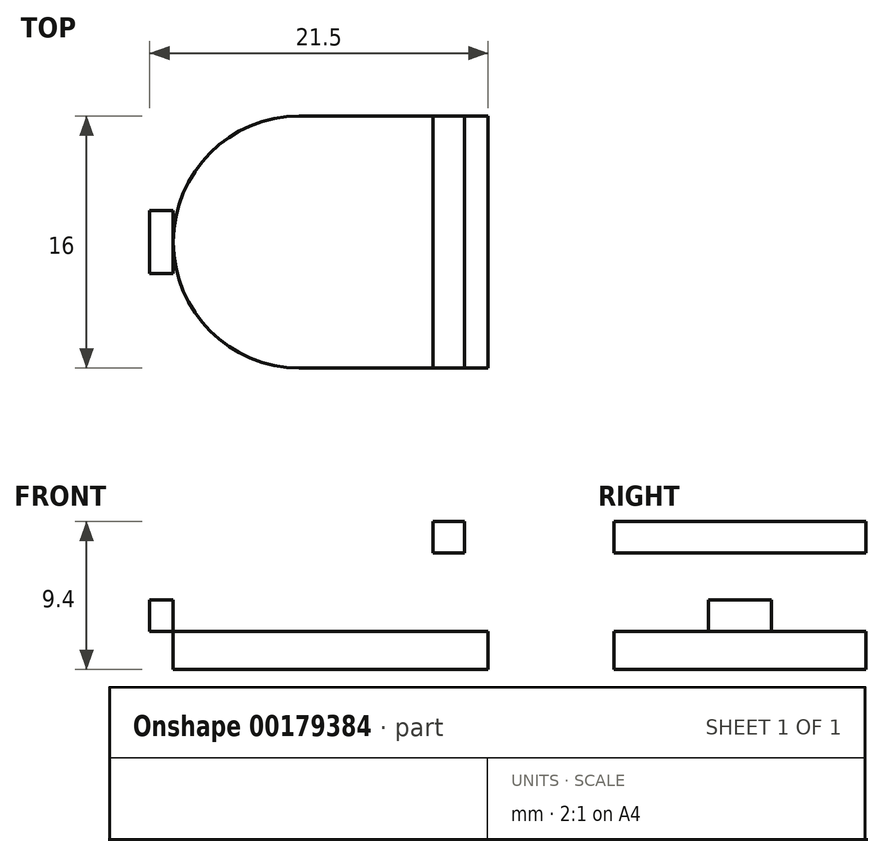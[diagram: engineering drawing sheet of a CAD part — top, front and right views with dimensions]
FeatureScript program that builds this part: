
annotation { "Feature Type Name" : "Feature", "Feature Type Description" : "" }
export const myFeature = defineFeature(function(context is Context, id is Id, definition is map)
    precondition{}
    {
        {
            var Q0;
            Q0=qCreatedBy(makeId("Front.planeOp"),FACE);
            var sketch = newSketch(context, id + "F0", { "sketchPlane" : qUnion([Q0])});
            skLineSegment(sketch, "E0.bottom", {"start": v(6, -1.2) * mm, "end": v(-6, -1.2) * mm});
            skLineSegment(sketch, "E0.top", {"start": v(6, 1.2) * mm, "end": v(-6, 1.2) * mm});
            skLineSegment(sketch, "E0.left", {"start": v(6, -1.2) * mm, "end": v(6, 1.2) * mm});
            skLineSegment(sketch, "E0.right", {"start": v(-6, -1.2) * mm, "end": v(-6, 1.2) * mm});
            skPoint(sketch, "E0.middle", {"position": v(0, 0) * mm});
            skLineSegment(sketch, "E1.bottom", {"start": v(6, 1.2) * mm, "end": v(4.5, 1.2) * mm});
            skLineSegment(sketch, "E1.top", {"start": v(6, 8.2) * mm, "end": v(4.5, 8.2) * mm});
            skLineSegment(sketch, "E1.left", {"start": v(6, 1.2) * mm, "end": v(6, 8.2) * mm});
            skLineSegment(sketch, "E1.right", {"start": v(4.5, 1.2) * mm, "end": v(4.5, 8.2) * mm});
            skLineSegment(sketch, "E2.bottom", {"start": v(4.5, 8.2) * mm, "end": v(2.5, 8.2) * mm});
            skLineSegment(sketch, "E2.top", {"start": v(4.5, 6.2) * mm, "end": v(2.5, 6.2) * mm});
            skLineSegment(sketch, "E2.left", {"start": v(4.5, 8.2) * mm, "end": v(4.5, 6.2) * mm});
            skLineSegment(sketch, "E2.right", {"start": v(2.5, 8.2) * mm, "end": v(2.5, 6.2) * mm});
            skLineSegment(sketch, "E3.bottom", {"start": v(-6, -1.2) * mm, "end": v(-14, -1.2) * mm});
            skLineSegment(sketch, "E3.top", {"start": v(-6, 1.2) * mm, "end": v(-14, 1.2) * mm});
            skLineSegment(sketch, "E3.right", {"start": v(-14, -1.2) * mm, "end": v(-14, 1.2) * mm});
            skLineSegment(sketch, "E4.bottom", {"start": v(-14, 1.2) * mm, "end": v(-11, 1.2) * mm});
            skLineSegment(sketch, "E4.top", {"start": v(-14, 3.2) * mm, "end": v(-11, 3.2) * mm});
            skLineSegment(sketch, "E4.left", {"start": v(-14, 1.2) * mm, "end": v(-14, 3.2) * mm});
            skLineSegment(sketch, "E4.right", {"start": v(-11, 1.2) * mm, "end": v(-11, 3.2) * mm});
            skLineSegment(sketch, "E5.bottom", {"start": v(-14, 1.2) * mm, "end": v(-15.5, 1.2) * mm});
            skLineSegment(sketch, "E5.top", {"start": v(-14, 3.2) * mm, "end": v(-15.5, 3.2) * mm});
            skLineSegment(sketch, "E5.right", {"start": v(-15.5, 1.2) * mm, "end": v(-15.5, 3.2) * mm});
            skSolve(sketch);
        }
        {
            var Q0;
            Q0=makeQuery(id+"F0.imprint","IMPRINT",FACE,{"disambiguationData":[TD([[makeQuery(id+"F0.imprint","IMPRINT",EDGE,{"derivedFrom":sQuery(id+"F0.wireOp",EDGE,"E2.bottom")}),1.0]])]});
            var Q1;
            Q1=makeQuery(id+"F0.imprint","IMPRINT",FACE,{"disambiguationData":[TD([[makeQuery(id+"F0.imprint","IMPRINT",EDGE,{"derivedFrom":sQuery(id+"F0.wireOp",EDGE,"E1.bottom")}),-1.0]])]});
            var Q2;
            Q2=makeQuery(id+"F0.imprint","IMPRINT",FACE,{"disambiguationData":[TD([[makeQuery(id+"F0.imprint","IMPRINT",EDGE,{"derivedFrom":sQuery(id+"F0.wireOp",EDGE,"E0.bottom")}),-1.0]])]});
            extrude(context, id + "F1", {"entities" : qUnion([Q0, Q1, Q2]), "endBound" : BoundingType.SYMMETRIC, "depth" : 16 * mm});
        }
        {
            var Q0;
            Q0=makeQuery(id+"F0.imprint","IMPRINT",FACE,{"disambiguationData":[TD([[makeQuery(id+"F0.imprint","IMPRINT",EDGE,{"derivedFrom":sQuery(id+"F0.wireOp",EDGE,"E3.bottom")}),-1.0]])]});
            var Q1;
            Q1=sQuery(id+"F0.wireOp",EDGE,"E0.right");
            revolve(context, id + "F2", {"operationType" : NewBodyOperationType.ADD, "entities" : qUnion([Q0]), "axis" : qUnion([Q1]), "revolveType" : RevolveType.SYMMETRIC, "angle" : 180 * degree});
        }
        {
            var Q0;
            Q0=makeQuery(id+"F0.imprint","IMPRINT",FACE,{"disambiguationData":[TD([[makeQuery(id+"F0.imprint","IMPRINT",EDGE,{"derivedFrom":sQuery(id+"F0.wireOp",EDGE,"E5.bottom")}),-1.0]])]});
            var Q1;
            Q1=makeQuery(id+"F0.imprint","IMPRINT",FACE,{"disambiguationData":[TD([[makeQuery(id+"F0.imprint","IMPRINT",EDGE,{"derivedFrom":sQuery(id+"F0.wireOp",EDGE,"E4.bottom")}),1.0]])]});
            extrude(context, id + "F3", {"entities" : qUnion([Q0, Q1]), "operationType" : NewBodyOperationType.ADD, "endBound" : BoundingType.SYMMETRIC, "depth" : 4 * mm});
        }
    });
